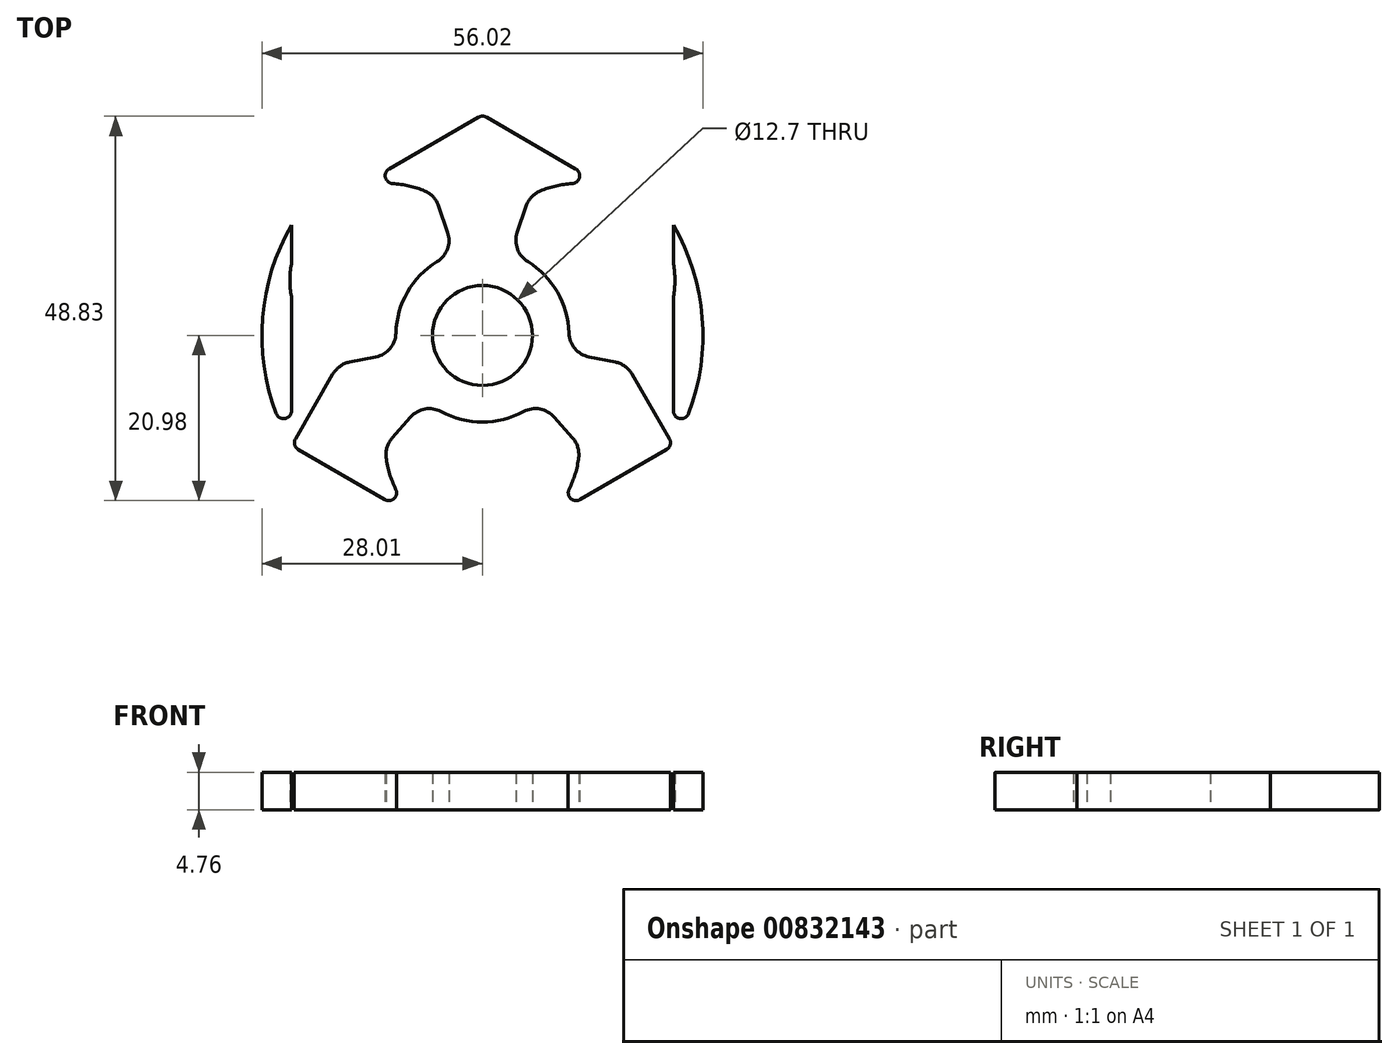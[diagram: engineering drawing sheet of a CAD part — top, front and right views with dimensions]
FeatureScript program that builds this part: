
annotation { "Feature Type Name" : "Feature", "Feature Type Description" : "" }
export const myFeature = defineFeature(function(context is Context, id is Id, definition is map)
    precondition{}
    {
        {
            var Q0;
            Q0=qCreatedBy(makeId("Top.planeOp"),FACE);
            var sketch = newSketch(context, id + "F0", { "sketchPlane" : qUnion([Q0])});
            skCircle(sketch, "E0", {"center": v(0, 0) * mm, "radius": 6.35 * mm});
            skCircle(sketch, "E1", {"center": v(0, 0) * mm, "radius": 11 * mm});
            skCircle(sketch, "E2", {"center": v(0, 0) * mm, "radius": 28 * mm});
            skLineSegment(sketch, "E3", {"start": v(0, 0) * mm, "end": v(0, 28) * mm});
            skLineSegment(sketch, "E4", {"start": v(0, 0) * mm, "end": v(24.26, -14) * mm});
            skLineSegment(sketch, "E5", {"start": v(0, 0) * mm, "end": v(-24.26, -14) * mm});
            skLineSegment(sketch, "E6", {"start": v(0, 28) * mm, "end": v(-24.26, -14) * mm});
            skLineSegment(sketch, "E7", {"start": v(0, 28) * mm, "end": v(24.26, -14) * mm});
            skLineSegment(sketch, "E8", {"start": v(-24.26, -14) * mm, "end": v(24.26, -14) * mm});
            skLineSegment(sketch, "E9", {"start": v(0, 0) * mm, "end": v(-24.26, 14) * mm});
            skLineSegment(sketch, "E10", {"start": v(0, 0) * mm, "end": v(24.26, 14) * mm});
            skLineSegment(sketch, "E11", {"start": v(0, 0) * mm, "end": v(0, -28) * mm});
            skCircle(sketch, "E12", {"center": v(12.13, 7) * mm, "radius": 12.32 * mm});
            skCircle(sketch, "E13", {"center": v(0, -14) * mm, "radius": 12.32 * mm});
            skCircle(sketch, "E14", {"center": v(-12.13, 7) * mm, "radius": 12.32 * mm});
            skLineSegment(sketch, "E15", {"start": v(-18.29, -3.67) * mm, "end": v(0, 0) * mm});
            skLineSegment(sketch, "E16", {"start": v(-12.32, -14) * mm, "end": v(0, 0) * mm});
            skLineSegment(sketch, "E17", {"start": v(-5.97, 17.67) * mm, "end": v(0, 0) * mm});
            skLineSegment(sketch, "E18", {"start": v(5.97, 17.67) * mm, "end": v(0, 0) * mm});
            skLineSegment(sketch, "E19", {"start": v(12.32, -14) * mm, "end": v(0, 0) * mm});
            skLineSegment(sketch, "E20", {"start": v(18.29, -3.67) * mm, "end": v(0, 0) * mm});
            skLineSegment(sketch, "E21", {"start": v(-24.26, 14) * mm, "end": v(-24.26, -14) * mm});
            skLineSegment(sketch, "E22", {"start": v(-24.26, 14) * mm, "end": v(0, 28) * mm});
            skLineSegment(sketch, "E23", {"start": v(0, 28) * mm, "end": v(24.26, 14) * mm});
            skLineSegment(sketch, "E24", {"start": v(24.26, 14) * mm, "end": v(24.26, -14) * mm});
            skLineSegment(sketch, "E25", {"start": v(24.26, -14) * mm, "end": v(0, -28) * mm});
            skLineSegment(sketch, "E26", {"start": v(0, -28) * mm, "end": v(-24.26, -14) * mm});
            skSolve(sketch);
        }
        {
            var Q0;
            {var subQ0=sQuery(id+"F0.wireOp",EDGE,"E3");var subQ1=sQuery(id+"F0.wireOp",EDGE,"E1");var subQ2=makeQuery(id+"F0.imprint","INTERSECT",VERTEX,{"derivedFrom":[subQ1,subQ0]});Q0=makeQuery(id+"F0.imprint","IMPRINT",FACE,{"disambiguationData":[TD([[makeQuery(id+"F0.imprint","IMPRINT",EDGE,{"disambiguationData":[TD([[subQ2,-1.0]])],"derivedFrom":subQ1}),-1.0]])]});}
            var Q1;
            {var subQ0=sQuery(id+"F0.wireOp",EDGE,"E12");var subQ1=sQuery(id+"F0.wireOp",EDGE,"E1");var subQ2=makeQuery(id+"F0.imprint","INTERSECT",VERTEX,{"disambiguationData":[OD(0.0)],"derivedFrom":[subQ1,subQ0]});Q1=makeQuery(id+"F0.imprint","IMPRINT",FACE,{"disambiguationData":[TD([[makeQuery(id+"F0.imprint","IMPRINT",EDGE,{"disambiguationData":[TD([[subQ2,-1.0]])],"derivedFrom":subQ1}),-1.0]])]});}
            var Q2;
            {var subQ0=sQuery(id+"F0.wireOp",EDGE,"E14");var subQ1=sQuery(id+"F0.wireOp",EDGE,"E1");var subQ2=makeQuery(id+"F0.imprint","INTERSECT",VERTEX,{"disambiguationData":[OD(1.0)],"derivedFrom":[subQ1,subQ0]});Q2=makeQuery(id+"F0.imprint","IMPRINT",FACE,{"disambiguationData":[TD([[makeQuery(id+"F0.imprint","IMPRINT",EDGE,{"disambiguationData":[TD([[subQ2,-1.0]])],"derivedFrom":subQ1}),-1.0]])]});}
            var Q3;
            {var subQ0=sQuery(id+"F0.wireOp",EDGE,"E5");var subQ1=sQuery(id+"F0.wireOp",EDGE,"E1");var subQ2=makeQuery(id+"F0.imprint","INTERSECT",VERTEX,{"derivedFrom":[subQ1,subQ0]});Q3=makeQuery(id+"F0.imprint","IMPRINT",FACE,{"disambiguationData":[TD([[makeQuery(id+"F0.imprint","IMPRINT",EDGE,{"disambiguationData":[TD([[subQ2,-1.0]])],"derivedFrom":subQ1}),-1.0]])]});}
            var Q4;
            {var subQ0=sQuery(id+"F0.wireOp",EDGE,"E13");var subQ1=sQuery(id+"F0.wireOp",EDGE,"E1");var subQ2=makeQuery(id+"F0.imprint","INTERSECT",VERTEX,{"disambiguationData":[OD(1.0)],"derivedFrom":[subQ1,subQ0]});Q4=makeQuery(id+"F0.imprint","IMPRINT",FACE,{"disambiguationData":[TD([[makeQuery(id+"F0.imprint","IMPRINT",EDGE,{"disambiguationData":[TD([[subQ2,-1.0]])],"derivedFrom":subQ1}),-1.0]])]});}
            var Q5;
            {var subQ0=sQuery(id+"F0.wireOp",EDGE,"E4");var subQ1=sQuery(id+"F0.wireOp",EDGE,"E1");var subQ2=makeQuery(id+"F0.imprint","INTERSECT",VERTEX,{"derivedFrom":[subQ1,subQ0]});Q5=makeQuery(id+"F0.imprint","IMPRINT",FACE,{"disambiguationData":[TD([[makeQuery(id+"F0.imprint","IMPRINT",EDGE,{"disambiguationData":[TD([[subQ2,-1.0]])],"derivedFrom":subQ1}),-1.0]])]});}
            var Q6;
            {var subQ0=sQuery(id+"F0.wireOp",EDGE,"E9");var subQ7=sQuery(id+"F0.wireOp",EDGE,"E0");var subQ9=makeQuery(id+"F0.imprint","INTERSECT",VERTEX,{"derivedFrom":[subQ7,subQ0]});Q6=makeQuery(id+"F0.imprint","IMPRINT",FACE,{"disambiguationData":[TD([[makeQuery(id+"F0.imprint","IMPRINT",EDGE,{"disambiguationData":[TD([[subQ9,-1.0]])],"derivedFrom":subQ7}),-1.0]])]});}
            var Q7;
            {var subQ1=sQuery(id+"F0.wireOp",EDGE,"E0");var subQ7=sQuery(id+"F0.wireOp",EDGE,"E12");var subQ8=makeQuery(id+"F0.imprint","INTERSECT",VERTEX,{"disambiguationData":[OD(0.0)],"derivedFrom":[subQ1,subQ7]});Q7=makeQuery(id+"F0.imprint","IMPRINT",FACE,{"disambiguationData":[TD([[makeQuery(id+"F0.imprint","IMPRINT",EDGE,{"disambiguationData":[TD([[subQ8,-1.0]])],"derivedFrom":subQ1}),-1.0]])]});}
            var Q8;
            {var subQ3=sQuery(id+"F0.wireOp",EDGE,"E14");var subQ5=sQuery(id+"F0.wireOp",EDGE,"E0");var subQ6=makeQuery(id+"F0.imprint","INTERSECT",VERTEX,{"disambiguationData":[OD(0.0)],"derivedFrom":[subQ5,subQ3]});Q8=makeQuery(id+"F0.imprint","IMPRINT",FACE,{"disambiguationData":[TD([[makeQuery(id+"F0.imprint","IMPRINT",EDGE,{"disambiguationData":[TD([[subQ6,1.0]])],"derivedFrom":subQ5}),-1.0]])]});}
            var Q9;
            {var subQ5=sQuery(id+"F0.wireOp",EDGE,"E10");var subQ6=sQuery(id+"F0.wireOp",EDGE,"E0");var subQ7=makeQuery(id+"F0.imprint","INTERSECT",VERTEX,{"derivedFrom":[subQ6,subQ5]});Q9=makeQuery(id+"F0.imprint","IMPRINT",FACE,{"disambiguationData":[TD([[makeQuery(id+"F0.imprint","IMPRINT",EDGE,{"disambiguationData":[TD([[subQ7,1.0]])],"derivedFrom":subQ6}),-1.0]])]});}
            var Q10;
            {var subQ0=sQuery(id+"F0.wireOp",EDGE,"E11");var subQ1=sQuery(id+"F0.wireOp",EDGE,"E0");var subQ2=makeQuery(id+"F0.imprint","INTERSECT",VERTEX,{"derivedFrom":[subQ1,subQ0]});Q10=makeQuery(id+"F0.imprint","IMPRINT",FACE,{"disambiguationData":[TD([[makeQuery(id+"F0.imprint","IMPRINT",EDGE,{"disambiguationData":[TD([[subQ2,-1.0]])],"derivedFrom":subQ1}),-1.0]])]});}
            var Q11;
            {var subQ3=sQuery(id+"F0.wireOp",EDGE,"E14");var subQ5=sQuery(id+"F0.wireOp",EDGE,"E0");var subQ6=makeQuery(id+"F0.imprint","INTERSECT",VERTEX,{"disambiguationData":[OD(1.0)],"derivedFrom":[subQ5,subQ3]});Q11=makeQuery(id+"F0.imprint","IMPRINT",FACE,{"disambiguationData":[TD([[makeQuery(id+"F0.imprint","IMPRINT",EDGE,{"disambiguationData":[TD([[subQ6,-1.0]])],"derivedFrom":subQ5}),-1.0]])]});}
            var Q12;
            {var subQ0=sQuery(id+"F0.wireOp",EDGE,"E14");var subQ1=sQuery(id+"F0.wireOp",EDGE,"E1");var subQ2=makeQuery(id+"F0.imprint","INTERSECT",VERTEX,{"disambiguationData":[OD(1.0)],"derivedFrom":[subQ1,subQ0]});Q12=makeQuery(id+"F0.imprint","IMPRINT",FACE,{"disambiguationData":[TD([[makeQuery(id+"F0.imprint","IMPRINT",EDGE,{"disambiguationData":[TD([[subQ2,-1.0]])],"derivedFrom":subQ1}),1.0]])]});}
            var Q13;
            {var subQ0=sQuery(id+"F0.wireOp",EDGE,"E5");var subQ1=sQuery(id+"F0.wireOp",EDGE,"E1");var subQ2=makeQuery(id+"F0.imprint","INTERSECT",VERTEX,{"derivedFrom":[subQ1,subQ0]});Q13=makeQuery(id+"F0.imprint","IMPRINT",FACE,{"disambiguationData":[TD([[makeQuery(id+"F0.imprint","IMPRINT",EDGE,{"disambiguationData":[TD([[subQ2,-1.0]])],"derivedFrom":subQ1}),1.0]])]});}
            var Q14;
            {var subQ0=sQuery(id+"F0.wireOp",EDGE,"E13");var subQ1=sQuery(id+"F0.wireOp",EDGE,"E0");var subQ2=makeQuery(id+"F0.imprint","INTERSECT",VERTEX,{"disambiguationData":[OD(0.0)],"derivedFrom":[subQ1,subQ0]});Q14=makeQuery(id+"F0.imprint","IMPRINT",FACE,{"disambiguationData":[TD([[makeQuery(id+"F0.imprint","IMPRINT",EDGE,{"disambiguationData":[TD([[subQ2,-1.0]])],"derivedFrom":subQ1}),-1.0]])]});}
            var Q15;
            {var subQ0=sQuery(id+"F0.wireOp",EDGE,"E5");var subQ1=sQuery(id+"F0.wireOp",EDGE,"E0");var subQ2=makeQuery(id+"F0.imprint","INTERSECT",VERTEX,{"derivedFrom":[subQ1,subQ0]});Q15=makeQuery(id+"F0.imprint","IMPRINT",FACE,{"disambiguationData":[TD([[makeQuery(id+"F0.imprint","IMPRINT",EDGE,{"disambiguationData":[TD([[subQ2,-1.0]])],"derivedFrom":subQ1}),-1.0]])]});}
            var Q16;
            {var subQ0=sQuery(id+"F0.wireOp",EDGE,"E3");var subQ1=sQuery(id+"F0.wireOp",EDGE,"E1");var subQ2=makeQuery(id+"F0.imprint","INTERSECT",VERTEX,{"derivedFrom":[subQ1,subQ0]});Q16=makeQuery(id+"F0.imprint","IMPRINT",FACE,{"disambiguationData":[TD([[makeQuery(id+"F0.imprint","IMPRINT",EDGE,{"disambiguationData":[TD([[subQ2,-1.0]])],"derivedFrom":subQ1}),1.0]])]});}
            var Q17;
            {var subQ0=sQuery(id+"F0.wireOp",EDGE,"E12");var subQ1=sQuery(id+"F0.wireOp",EDGE,"E1");var subQ2=makeQuery(id+"F0.imprint","INTERSECT",VERTEX,{"disambiguationData":[OD(0.0)],"derivedFrom":[subQ1,subQ0]});Q17=makeQuery(id+"F0.imprint","IMPRINT",FACE,{"disambiguationData":[TD([[makeQuery(id+"F0.imprint","IMPRINT",EDGE,{"disambiguationData":[TD([[subQ2,-1.0]])],"derivedFrom":subQ1}),1.0]])]});}
            var Q18;
            {var subQ0=sQuery(id+"F0.wireOp",EDGE,"E3");var subQ1=sQuery(id+"F0.wireOp",EDGE,"E0");var subQ2=makeQuery(id+"F0.imprint","INTERSECT",VERTEX,{"derivedFrom":[subQ1,subQ0]});Q18=makeQuery(id+"F0.imprint","IMPRINT",FACE,{"disambiguationData":[TD([[makeQuery(id+"F0.imprint","IMPRINT",EDGE,{"disambiguationData":[TD([[subQ2,-1.0]])],"derivedFrom":subQ1}),-1.0]])]});}
            var Q19;
            {var subQ0=sQuery(id+"F0.wireOp",EDGE,"E14");var subQ1=sQuery(id+"F0.wireOp",EDGE,"E0");var subQ2=makeQuery(id+"F0.imprint","INTERSECT",VERTEX,{"disambiguationData":[OD(0.0)],"derivedFrom":[subQ1,subQ0]});Q19=makeQuery(id+"F0.imprint","IMPRINT",FACE,{"disambiguationData":[TD([[makeQuery(id+"F0.imprint","IMPRINT",EDGE,{"disambiguationData":[TD([[subQ2,-1.0]])],"derivedFrom":subQ1}),-1.0]])]});}
            var Q20;
            {var subQ0=sQuery(id+"F0.wireOp",EDGE,"E4");var subQ1=sQuery(id+"F0.wireOp",EDGE,"E0");var subQ2=makeQuery(id+"F0.imprint","INTERSECT",VERTEX,{"derivedFrom":[subQ1,subQ0]});Q20=makeQuery(id+"F0.imprint","IMPRINT",FACE,{"disambiguationData":[TD([[makeQuery(id+"F0.imprint","IMPRINT",EDGE,{"disambiguationData":[TD([[subQ2,-1.0]])],"derivedFrom":subQ1}),-1.0]])]});}
            var Q21;
            {var subQ0=sQuery(id+"F0.wireOp",EDGE,"E12");var subQ1=sQuery(id+"F0.wireOp",EDGE,"E0");var subQ2=makeQuery(id+"F0.imprint","INTERSECT",VERTEX,{"disambiguationData":[OD(1.0)],"derivedFrom":[subQ1,subQ0]});Q21=makeQuery(id+"F0.imprint","IMPRINT",FACE,{"disambiguationData":[TD([[makeQuery(id+"F0.imprint","IMPRINT",EDGE,{"disambiguationData":[TD([[subQ2,-1.0]])],"derivedFrom":subQ1}),-1.0]])]});}
            var Q22;
            {var subQ0=sQuery(id+"F0.wireOp",EDGE,"E4");var subQ1=sQuery(id+"F0.wireOp",EDGE,"E1");var subQ2=makeQuery(id+"F0.imprint","INTERSECT",VERTEX,{"derivedFrom":[subQ1,subQ0]});Q22=makeQuery(id+"F0.imprint","IMPRINT",FACE,{"disambiguationData":[TD([[makeQuery(id+"F0.imprint","IMPRINT",EDGE,{"disambiguationData":[TD([[subQ2,-1.0]])],"derivedFrom":subQ1}),1.0]])]});}
            var Q23;
            {var subQ0=sQuery(id+"F0.wireOp",EDGE,"E13");var subQ1=sQuery(id+"F0.wireOp",EDGE,"E1");var subQ2=makeQuery(id+"F0.imprint","INTERSECT",VERTEX,{"disambiguationData":[OD(1.0)],"derivedFrom":[subQ1,subQ0]});Q23=makeQuery(id+"F0.imprint","IMPRINT",FACE,{"disambiguationData":[TD([[makeQuery(id+"F0.imprint","IMPRINT",EDGE,{"disambiguationData":[TD([[subQ2,-1.0]])],"derivedFrom":subQ1}),1.0]])]});}
            var Q24;
            {var subQ0=sQuery(id+"F0.wireOp",EDGE,"E15");var subQ1=sQuery(id+"F0.wireOp",EDGE,"E1");var subQ2=makeQuery(id+"F0.imprint","INTERSECT",VERTEX,{"derivedFrom":[subQ1,subQ0]});Q24=makeQuery(id+"F0.imprint","IMPRINT",FACE,{"disambiguationData":[TD([[makeQuery(id+"F0.imprint","IMPRINT",EDGE,{"disambiguationData":[TD([[subQ2,-1.0]])],"derivedFrom":subQ1}),-1.0]])]});}
            var Q25;
            {var subQ5=sQuery(id+"F0.wireOp",EDGE,"E0");var subQ7=sQuery(id+"F0.wireOp",EDGE,"E15");var subQ9=makeQuery(id+"F0.imprint","INTERSECT",VERTEX,{"derivedFrom":[subQ5,subQ7]});Q25=makeQuery(id+"F0.imprint","IMPRINT",FACE,{"disambiguationData":[TD([[makeQuery(id+"F0.imprint","IMPRINT",EDGE,{"disambiguationData":[TD([[subQ9,-1.0]])],"derivedFrom":subQ5}),-1.0]])]});}
            var Q26;
            {var subQ0=sQuery(id+"F0.wireOp",EDGE,"E13");var subQ1=sQuery(id+"F0.wireOp",EDGE,"E1");var subQ2=makeQuery(id+"F0.imprint","INTERSECT",VERTEX,{"disambiguationData":[OD(0.0)],"derivedFrom":[subQ1,subQ0]});Q26=makeQuery(id+"F0.imprint","IMPRINT",FACE,{"disambiguationData":[TD([[makeQuery(id+"F0.imprint","IMPRINT",EDGE,{"disambiguationData":[TD([[subQ2,-1.0]])],"derivedFrom":subQ1}),-1.0]])]});}
            var Q27;
            {var subQ0=sQuery(id+"F0.wireOp",EDGE,"E19");var subQ1=sQuery(id+"F0.wireOp",EDGE,"E1");var subQ2=makeQuery(id+"F0.imprint","INTERSECT",VERTEX,{"derivedFrom":[subQ1,subQ0]});Q27=makeQuery(id+"F0.imprint","IMPRINT",FACE,{"disambiguationData":[TD([[makeQuery(id+"F0.imprint","IMPRINT",EDGE,{"disambiguationData":[TD([[subQ2,-1.0]])],"derivedFrom":subQ1}),-1.0]])]});}
            var Q28;
            {var subQ5=sQuery(id+"F0.wireOp",EDGE,"E19");var subQ6=sQuery(id+"F0.wireOp",EDGE,"E0");var subQ7=makeQuery(id+"F0.imprint","INTERSECT",VERTEX,{"derivedFrom":[subQ6,subQ5]});Q28=makeQuery(id+"F0.imprint","IMPRINT",FACE,{"disambiguationData":[TD([[makeQuery(id+"F0.imprint","IMPRINT",EDGE,{"disambiguationData":[TD([[subQ7,-1.0]])],"derivedFrom":subQ6}),-1.0]])]});}
            var Q29;
            {var subQ0=sQuery(id+"F0.wireOp",EDGE,"E13");var subQ1=sQuery(id+"F0.wireOp",EDGE,"E0");var subQ2=makeQuery(id+"F0.imprint","INTERSECT",VERTEX,{"disambiguationData":[OD(1.0)],"derivedFrom":[subQ1,subQ0]});Q29=makeQuery(id+"F0.imprint","IMPRINT",FACE,{"disambiguationData":[TD([[makeQuery(id+"F0.imprint","IMPRINT",EDGE,{"disambiguationData":[TD([[subQ2,-1.0]])],"derivedFrom":subQ1}),-1.0]])]});}
            var Q30;
            {var subQ0=sQuery(id+"F0.wireOp",EDGE,"E12");var subQ1=sQuery(id+"F0.wireOp",EDGE,"E1");var subQ2=makeQuery(id+"F0.imprint","INTERSECT",VERTEX,{"disambiguationData":[OD(1.0)],"derivedFrom":[subQ1,subQ0]});Q30=makeQuery(id+"F0.imprint","IMPRINT",FACE,{"disambiguationData":[TD([[makeQuery(id+"F0.imprint","IMPRINT",EDGE,{"disambiguationData":[TD([[subQ2,-1.0]])],"derivedFrom":subQ1}),-1.0]])]});}
            var Q31;
            {var subQ0=sQuery(id+"F0.wireOp",EDGE,"E18");var subQ1=sQuery(id+"F0.wireOp",EDGE,"E0");var subQ2=makeQuery(id+"F0.imprint","INTERSECT",VERTEX,{"derivedFrom":[subQ1,subQ0]});Q31=makeQuery(id+"F0.imprint","IMPRINT",FACE,{"disambiguationData":[TD([[makeQuery(id+"F0.imprint","IMPRINT",EDGE,{"disambiguationData":[TD([[subQ2,1.0]])],"derivedFrom":subQ1}),-1.0]])]});}
            var Q32;
            {var subQ0=sQuery(id+"F0.wireOp",EDGE,"E17");var subQ1=sQuery(id+"F0.wireOp",EDGE,"E0");var subQ2=makeQuery(id+"F0.imprint","INTERSECT",VERTEX,{"derivedFrom":[subQ1,subQ0]});Q32=makeQuery(id+"F0.imprint","IMPRINT",FACE,{"disambiguationData":[TD([[makeQuery(id+"F0.imprint","IMPRINT",EDGE,{"disambiguationData":[TD([[subQ2,-1.0]])],"derivedFrom":subQ1}),-1.0]])]});}
            var Q33;
            {var subQ0=sQuery(id+"F0.wireOp",EDGE,"E16");var subQ1=sQuery(id+"F0.wireOp",EDGE,"E0");var subQ2=makeQuery(id+"F0.imprint","INTERSECT",VERTEX,{"derivedFrom":[subQ1,subQ0]});Q33=makeQuery(id+"F0.imprint","IMPRINT",FACE,{"disambiguationData":[TD([[makeQuery(id+"F0.imprint","IMPRINT",EDGE,{"disambiguationData":[TD([[subQ2,-1.0]])],"derivedFrom":subQ1}),-1.0]])]});}
            var Q34;
            {var subQ0=sQuery(id+"F0.wireOp",EDGE,"E14");var subQ1=sQuery(id+"F0.wireOp",EDGE,"E1");var subQ2=makeQuery(id+"F0.imprint","INTERSECT",VERTEX,{"disambiguationData":[OD(0.0)],"derivedFrom":[subQ1,subQ0]});Q34=makeQuery(id+"F0.imprint","IMPRINT",FACE,{"disambiguationData":[TD([[makeQuery(id+"F0.imprint","IMPRINT",EDGE,{"disambiguationData":[TD([[subQ2,-1.0]])],"derivedFrom":subQ1}),-1.0]])]});}
            var Q35;
            {var subQ0=sQuery(id+"F0.wireOp",EDGE,"E18");var subQ1=sQuery(id+"F0.wireOp",EDGE,"E1");var subQ2=makeQuery(id+"F0.imprint","INTERSECT",VERTEX,{"derivedFrom":[subQ1,subQ0]});Q35=makeQuery(id+"F0.imprint","IMPRINT",FACE,{"disambiguationData":[TD([[makeQuery(id+"F0.imprint","IMPRINT",EDGE,{"disambiguationData":[TD([[subQ2,-1.0]])],"derivedFrom":subQ1}),-1.0]])]});}
            var Q36;
            {var subQ0=sQuery(id+"F0.wireOp",EDGE,"E21");var subQ3=sQuery(id+"F0.wireOp",EDGE,"E14");var subQ5=makeQuery(id+"F0.imprint","INTERSECT",VERTEX,{"disambiguationData":[OD(1.0)],"derivedFrom":[subQ3,subQ0]});Q36=makeQuery(id+"F0.imprint","IMPRINT",FACE,{"disambiguationData":[TD([[makeQuery(id+"F0.imprint","IMPRINT",EDGE,{"disambiguationData":[TD([[subQ5,-1.0]])],"derivedFrom":subQ3}),-1.0]])]});}
            var Q37;
            {var subQ0=sQuery(id+"F0.wireOp",EDGE,"E26");var subQ3=sQuery(id+"F0.wireOp",EDGE,"E13");var subQ5=makeQuery(id+"F0.imprint","INTERSECT",VERTEX,{"disambiguationData":[OD(0.0)],"derivedFrom":[subQ3,subQ0]});Q37=makeQuery(id+"F0.imprint","IMPRINT",FACE,{"disambiguationData":[TD([[makeQuery(id+"F0.imprint","IMPRINT",EDGE,{"disambiguationData":[TD([[subQ5,1.0]])],"derivedFrom":subQ3}),-1.0]])]});}
            var Q38;
            {var subQ0=sQuery(id+"F0.wireOp",EDGE,"E25");var subQ3=sQuery(id+"F0.wireOp",EDGE,"E13");var subQ5=makeQuery(id+"F0.imprint","INTERSECT",VERTEX,{"disambiguationData":[OD(1.0)],"derivedFrom":[subQ3,subQ0]});Q38=makeQuery(id+"F0.imprint","IMPRINT",FACE,{"disambiguationData":[TD([[makeQuery(id+"F0.imprint","IMPRINT",EDGE,{"disambiguationData":[TD([[subQ5,-1.0]])],"derivedFrom":subQ3}),-1.0]])]});}
            var Q39;
            {var subQ0=sQuery(id+"F0.wireOp",EDGE,"E24");var subQ3=sQuery(id+"F0.wireOp",EDGE,"E12");var subQ5=makeQuery(id+"F0.imprint","INTERSECT",VERTEX,{"disambiguationData":[OD(1.0)],"derivedFrom":[subQ3,subQ0]});Q39=makeQuery(id+"F0.imprint","IMPRINT",FACE,{"disambiguationData":[TD([[makeQuery(id+"F0.imprint","IMPRINT",EDGE,{"disambiguationData":[TD([[subQ5,1.0]])],"derivedFrom":subQ3}),-1.0]])]});}
            var Q40;
            {var subQ0=sQuery(id+"F0.wireOp",EDGE,"E23");var subQ3=sQuery(id+"F0.wireOp",EDGE,"E12");var subQ5=makeQuery(id+"F0.imprint","INTERSECT",VERTEX,{"disambiguationData":[OD(1.0)],"derivedFrom":[subQ3,subQ0]});Q40=makeQuery(id+"F0.imprint","IMPRINT",FACE,{"disambiguationData":[TD([[makeQuery(id+"F0.imprint","IMPRINT",EDGE,{"disambiguationData":[TD([[subQ5,-1.0]])],"derivedFrom":subQ3}),-1.0]])]});}
            var Q41;
            {var subQ0=sQuery(id+"F0.wireOp",EDGE,"E22");var subQ3=sQuery(id+"F0.wireOp",EDGE,"E14");var subQ5=makeQuery(id+"F0.imprint","INTERSECT",VERTEX,{"disambiguationData":[OD(0.0)],"derivedFrom":[subQ3,subQ0]});Q41=makeQuery(id+"F0.imprint","IMPRINT",FACE,{"disambiguationData":[TD([[makeQuery(id+"F0.imprint","IMPRINT",EDGE,{"disambiguationData":[TD([[subQ5,1.0]])],"derivedFrom":subQ3}),-1.0]])]});}
            extrude(context, id + "F1", {"entities" : qUnion([Q0, Q1, Q2, Q3, Q4, Q5, Q6, Q7, Q8, Q9, Q10, Q11, Q12, Q13, Q14, Q15, Q16, Q17, Q18, Q19, Q20, Q21, Q22, Q23, Q24, Q25, Q26, Q27, Q28, Q29, Q30, Q31, Q32, Q33, Q34, Q35, Q36, Q37, Q38, Q39, Q40, Q41]), "depth" : 4.76 * mm, "offsetDistance" : 25.4 * mm});
        }
        {
            var Q0;
            Q0=makeQuery(id+"F1.opExtrude","SWEPT_EDGE",EDGE,{"disambiguationData":[OSD([sQuery(id+"F0.wireOp",EDGE,"E6"),sQuery(id+"F0.wireOp",EDGE,"E14"),sQuery(id+"F0.wireOp",EDGE,"E17")])]});
            var Q1;
            Q1=makeQuery(id+"F1.opExtrude","SWEPT_EDGE",EDGE,{"disambiguationData":[OSD([sQuery(id+"F0.wireOp",EDGE,"E7"),sQuery(id+"F0.wireOp",EDGE,"E12"),sQuery(id+"F0.wireOp",EDGE,"E18")])]});
            var Q2;
            Q2=makeQuery(id+"F1.opExtrude","SWEPT_EDGE",EDGE,{"disambiguationData":[OSD([sQuery(id+"F0.wireOp",EDGE,"E1"),sQuery(id+"F0.wireOp",EDGE,"E16")])]});
            var Q3;
            Q3=makeQuery(id+"F1.opExtrude","SWEPT_EDGE",EDGE,{"disambiguationData":[OSD([sQuery(id+"F0.wireOp",EDGE,"E1"),sQuery(id+"F0.wireOp",EDGE,"E19")])]});
            var Q4;
            Q4=makeQuery(id+"F1.opExtrude","SWEPT_EDGE",EDGE,{"disambiguationData":[OSD([sQuery(id+"F0.wireOp",EDGE,"E6"),sQuery(id+"F0.wireOp",EDGE,"E14"),sQuery(id+"F0.wireOp",EDGE,"E15")])]});
            var Q5;
            Q5=makeQuery(id+"F1.opExtrude","SWEPT_EDGE",EDGE,{"disambiguationData":[OSD([sQuery(id+"F0.wireOp",EDGE,"E7"),sQuery(id+"F0.wireOp",EDGE,"E12"),sQuery(id+"F0.wireOp",EDGE,"E20")])]});
            var Q6;
            Q6=makeQuery(id+"F1.opExtrude","SWEPT_EDGE",EDGE,{"disambiguationData":[OSD([sQuery(id+"F0.wireOp",EDGE,"E1"),sQuery(id+"F0.wireOp",EDGE,"E18")])]});
            var Q7;
            Q7=makeQuery(id+"F1.opExtrude","SWEPT_EDGE",EDGE,{"disambiguationData":[OSD([sQuery(id+"F0.wireOp",EDGE,"E1"),sQuery(id+"F0.wireOp",EDGE,"E20")])]});
            var Q8;
            Q8=makeQuery(id+"F1.opExtrude","SWEPT_EDGE",EDGE,{"disambiguationData":[OSD([sQuery(id+"F0.wireOp",EDGE,"E8"),sQuery(id+"F0.wireOp",EDGE,"E13"),sQuery(id+"F0.wireOp",EDGE,"E16")])]});
            var Q9;
            Q9=makeQuery(id+"F1.opExtrude","SWEPT_EDGE",EDGE,{"disambiguationData":[OSD([sQuery(id+"F0.wireOp",EDGE,"E8"),sQuery(id+"F0.wireOp",EDGE,"E13"),sQuery(id+"F0.wireOp",EDGE,"E19")])]});
            var Q10;
            Q10=makeQuery(id+"F1.opExtrude","SWEPT_EDGE",EDGE,{"disambiguationData":[OSD([sQuery(id+"F0.wireOp",EDGE,"E1"),sQuery(id+"F0.wireOp",EDGE,"E15")])]});
            var Q11;
            Q11=makeQuery(id+"F1.opExtrude","SWEPT_EDGE",EDGE,{"disambiguationData":[OSD([sQuery(id+"F0.wireOp",EDGE,"E1"),sQuery(id+"F0.wireOp",EDGE,"E17")])]});
            fillet(context, id + "F2", {"entities" : qUnion([Q0, Q1, Q2, Q3, Q4, Q5, Q6, Q7, Q8, Q9, Q10, Q11]), "radius" : 3.17 * mm, "tangentPropagation" : true, "allowEdgeOverflow" : false});
        }
        {
            var Q0;
            Q0=makeQuery(id+"F1.opExtrude","SWEPT_EDGE",EDGE,{"disambiguationData":[OSD([sQuery(id+"F0.wireOp",EDGE,"E14"),sQuery(id+"F0.wireOp",EDGE,"E21")])]});
            var Q1;
            Q1=makeQuery(id+"F1.opExtrude","SWEPT_EDGE",EDGE,{"disambiguationData":[OSD([sQuery(id+"F0.wireOp",EDGE,"E12"),sQuery(id+"F0.wireOp",EDGE,"E24")])]});
            var Q2;
            Q2=makeQuery(id+"F1.opExtrude","SWEPT_EDGE",EDGE,{"disambiguationData":[OSD([sQuery(id+"F0.wireOp",EDGE,"E12"),sQuery(id+"F0.wireOp",EDGE,"E23")])]});
            var Q3;
            Q3=makeQuery(id+"F1.opExtrude","SWEPT_EDGE",EDGE,{"disambiguationData":[OSD([sQuery(id+"F0.wireOp",EDGE,"E14"),sQuery(id+"F0.wireOp",EDGE,"E22")])]});
            var Q4;
            Q4=makeQuery(id+"F1.opExtrude","SWEPT_EDGE",EDGE,{"disambiguationData":[OSD([sQuery(id+"F0.wireOp",EDGE,"E13"),sQuery(id+"F0.wireOp",EDGE,"E25")])]});
            var Q5;
            Q5=makeQuery(id+"F1.opExtrude","SWEPT_EDGE",EDGE,{"disambiguationData":[OSD([sQuery(id+"F0.wireOp",EDGE,"E13"),sQuery(id+"F0.wireOp",EDGE,"E26")])]});
            var Q6;
            Q6=makeQuery(id+"F1.opExtrude","SWEPT_EDGE",EDGE,{"disambiguationData":[OSD([sQuery(id+"F0.wireOp",EDGE,"E2"),sQuery(id+"F0.wireOp",EDGE,"E3"),sQuery(id+"F0.wireOp",EDGE,"E6"),sQuery(id+"F0.wireOp",EDGE,"E7"),sQuery(id+"F0.wireOp",EDGE,"E22"),sQuery(id+"F0.wireOp",EDGE,"E23")])]});
            var Q7;
            Q7=makeQuery(id+"F1.opExtrude","SWEPT_EDGE",EDGE,{"disambiguationData":[OSD([sQuery(id+"F0.wireOp",EDGE,"E2"),sQuery(id+"F0.wireOp",EDGE,"E4"),sQuery(id+"F0.wireOp",EDGE,"E7"),sQuery(id+"F0.wireOp",EDGE,"E8"),sQuery(id+"F0.wireOp",EDGE,"E24"),sQuery(id+"F0.wireOp",EDGE,"E25")])]});
            var Q8;
            Q8=makeQuery(id+"F1.opExtrude","SWEPT_EDGE",EDGE,{"disambiguationData":[OSD([sQuery(id+"F0.wireOp",EDGE,"E2"),sQuery(id+"F0.wireOp",EDGE,"E5"),sQuery(id+"F0.wireOp",EDGE,"E6"),sQuery(id+"F0.wireOp",EDGE,"E8"),sQuery(id+"F0.wireOp",EDGE,"E21"),sQuery(id+"F0.wireOp",EDGE,"E26")])]});
            fillet(context, id + "F3", {"entities" : qUnion([Q0, Q1, Q2, Q3, Q4, Q5, Q6, Q7, Q8]), "radius" : 1 * mm, "tangentPropagation" : true, "allowEdgeOverflow" : false});
        }
    });
